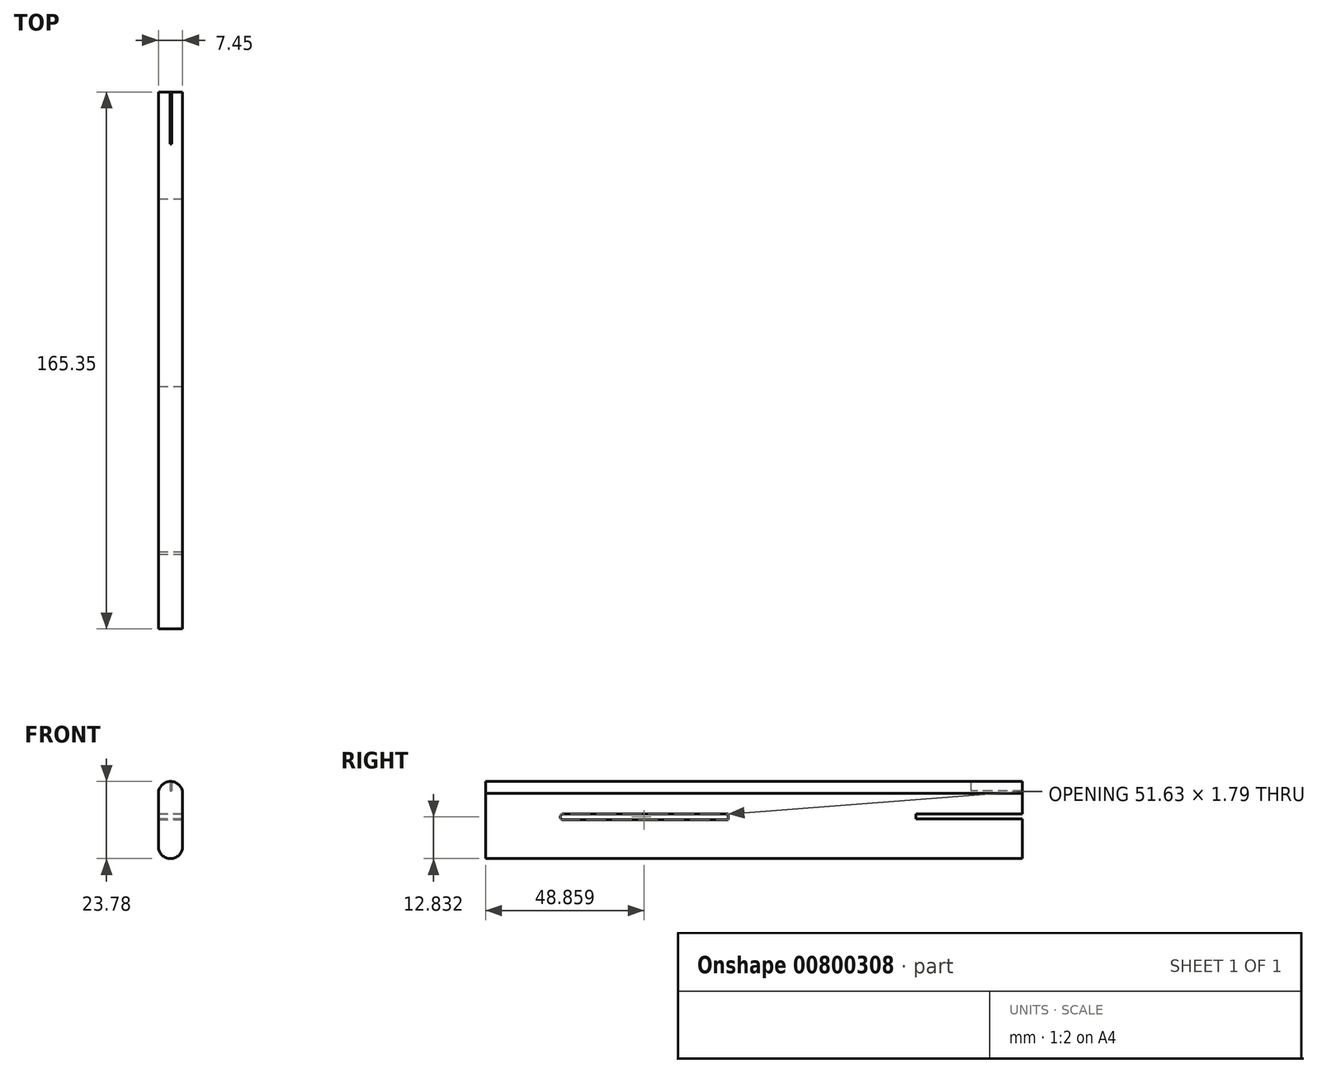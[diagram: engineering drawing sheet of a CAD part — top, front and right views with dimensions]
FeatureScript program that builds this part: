
annotation { "Feature Type Name" : "Feature", "Feature Type Description" : "" }
export const myFeature = defineFeature(function(context is Context, id is Id, definition is map)
    precondition{}
    {
        {
            var Q0;
            Q0=qCreatedBy(makeId("Front.planeOp"),FACE);
            var sketch = newSketch(context, id + "F0", { "sketchPlane" : qUnion([Q0])});
            skArc(sketch, "E0", {"start": v(3.64, 16.44) * mm, "mid": v(-0.08, 20.05) * mm, "end": v(-3.8, 16.44) * mm});
            skLineSegment(sketch, "E1.bottom", {"start": v(-3.8, 16.44) * mm, "end": v(3.64, 16.44) * mm});
            skLineSegment(sketch, "E1.top", {"start": v(-3.8, 0) * mm, "end": v(3.64, 0) * mm});
            skLineSegment(sketch, "E1.left", {"start": v(-3.8, 16.44) * mm, "end": v(-3.8, 0) * mm});
            skLineSegment(sketch, "E1.right", {"start": v(3.64, 16.44) * mm, "end": v(3.64, 0) * mm});
            skArc(sketch, "E2", {"start": v(-3.8, 0) * mm, "mid": v(-0.08, -3.73) * mm, "end": v(3.64, 0) * mm});
            skSolve(sketch);
        }
        {
            var Q0;
            Q0 = qSketchRegion(id + "F0", true);
            extrude(context, id + "F1", {"entities" : qUnion([Q0]), "oppositeDirection" : true, "depth" : 165.35 * mm, "offsetDistance" : 25.4 * mm});
        }
        {
            var Q0;
            Q0=qCreatedBy(makeId("Right.planeOp"),FACE);
            cPlane(context, id + "F2", {"entities" : qUnion([Q0]), "cplaneType" : CPlaneType.OFFSET, "offset" : 139.7 * mm, "width" : 152.4 * mm, "height" : 152.4 * mm});
        }
        {
            var Q0;
            Q0=qCreatedBy(id+"F2.planeOp",FACE);
            var sketch = newSketch(context, id + "F3", { "sketchPlane" : qUnion([Q0])});
            skArc(sketch, "E3", {"start": v(23.74, 10) * mm, "mid": v(23.04, 9.1) * mm, "end": v(23.74, 8.2) * mm});
            skLineSegment(sketch, "E4.bottom", {"start": v(23.74, 8.2) * mm, "end": v(74.68, 8.2) * mm});
            skLineSegment(sketch, "E4.top", {"start": v(23.74, 10) * mm, "end": v(74.68, 10) * mm});
            skLineSegment(sketch, "E4.left", {"start": v(23.74, 8.2) * mm, "end": v(23.74, 10) * mm});
            skLineSegment(sketch, "E4.right", {"start": v(74.68, 8.2) * mm, "end": v(74.68, 10) * mm});
            skSolve(sketch);
        }
        {
            var Q0;
            Q0 = qSketchRegion(id + "F3", true);
            extrude(context, id + "F4", {"entities" : qUnion([Q0]), "operationType" : NewBodyOperationType.REMOVE, "oppositeDirection" : true, "depth" : 232.4 * mm, "offsetDistance" : 25.4 * mm});
        }
        {
            var Q0;
            Q0=qCreatedBy(makeId("Front.planeOp"),FACE);
            cPlane(context, id + "F5", {"entities" : qUnion([Q0]), "cplaneType" : CPlaneType.OFFSET, "offset" : 149.35 * mm, "oppositeDirection" : true, "width" : 152.4 * mm, "height" : 152.4 * mm});
        }
        {
            var Q0;
            Q0=qCreatedBy(id+"F5.planeOp",FACE);
            var sketch = newSketch(context, id + "F6", { "sketchPlane" : qUnion([Q0])});
            skLineSegment(sketch, "E5.bottom", {"start": v(-0.27, 20.6) * mm, "end": v(0.24, 20.6) * mm});
            skLineSegment(sketch, "E5.top", {"start": v(-0.27, 17.2) * mm, "end": v(0.24, 17.2) * mm});
            skLineSegment(sketch, "E5.left", {"start": v(-0.27, 20.6) * mm, "end": v(-0.27, 17.2) * mm});
            skLineSegment(sketch, "E5.right", {"start": v(0.24, 20.6) * mm, "end": v(0.24, 17.2) * mm});
            skSolve(sketch);
        }
        {
            var Q0;
            Q0 = qSketchRegion(id + "F6", true);
            extrude(context, id + "F7", {"entities" : qUnion([Q0]), "operationType" : NewBodyOperationType.REMOVE, "oppositeDirection" : true, "depth" : 43.6 * mm, "offsetDistance" : 25.4 * mm});
        }
        {
            var Q0;
            Q0=qCreatedBy(id+"F2.planeOp",FACE);
            var sketch = newSketch(context, id + "F8", { "sketchPlane" : qUnion([Q0])});
            skLineSegment(sketch, "E6.bottom", {"start": v(169.69, 9.97) * mm, "end": v(132.5, 9.97) * mm});
            skLineSegment(sketch, "E6.top", {"start": v(169.69, 8.48) * mm, "end": v(132.5, 8.48) * mm});
            skLineSegment(sketch, "E6.left", {"start": v(169.69, 9.97) * mm, "end": v(169.69, 8.48) * mm});
            skLineSegment(sketch, "E6.right", {"start": v(132.5, 9.97) * mm, "end": v(132.5, 8.48) * mm});
            skSolve(sketch);
        }
        {
            var Q0;
            Q0 = qSketchRegion(id + "F8", true);
            extrude(context, id + "F9", {"entities" : qUnion([Q0]), "operationType" : NewBodyOperationType.REMOVE, "oppositeDirection" : true, "depth" : 232.4 * mm, "offsetDistance" : 25.4 * mm});
        }
    });
